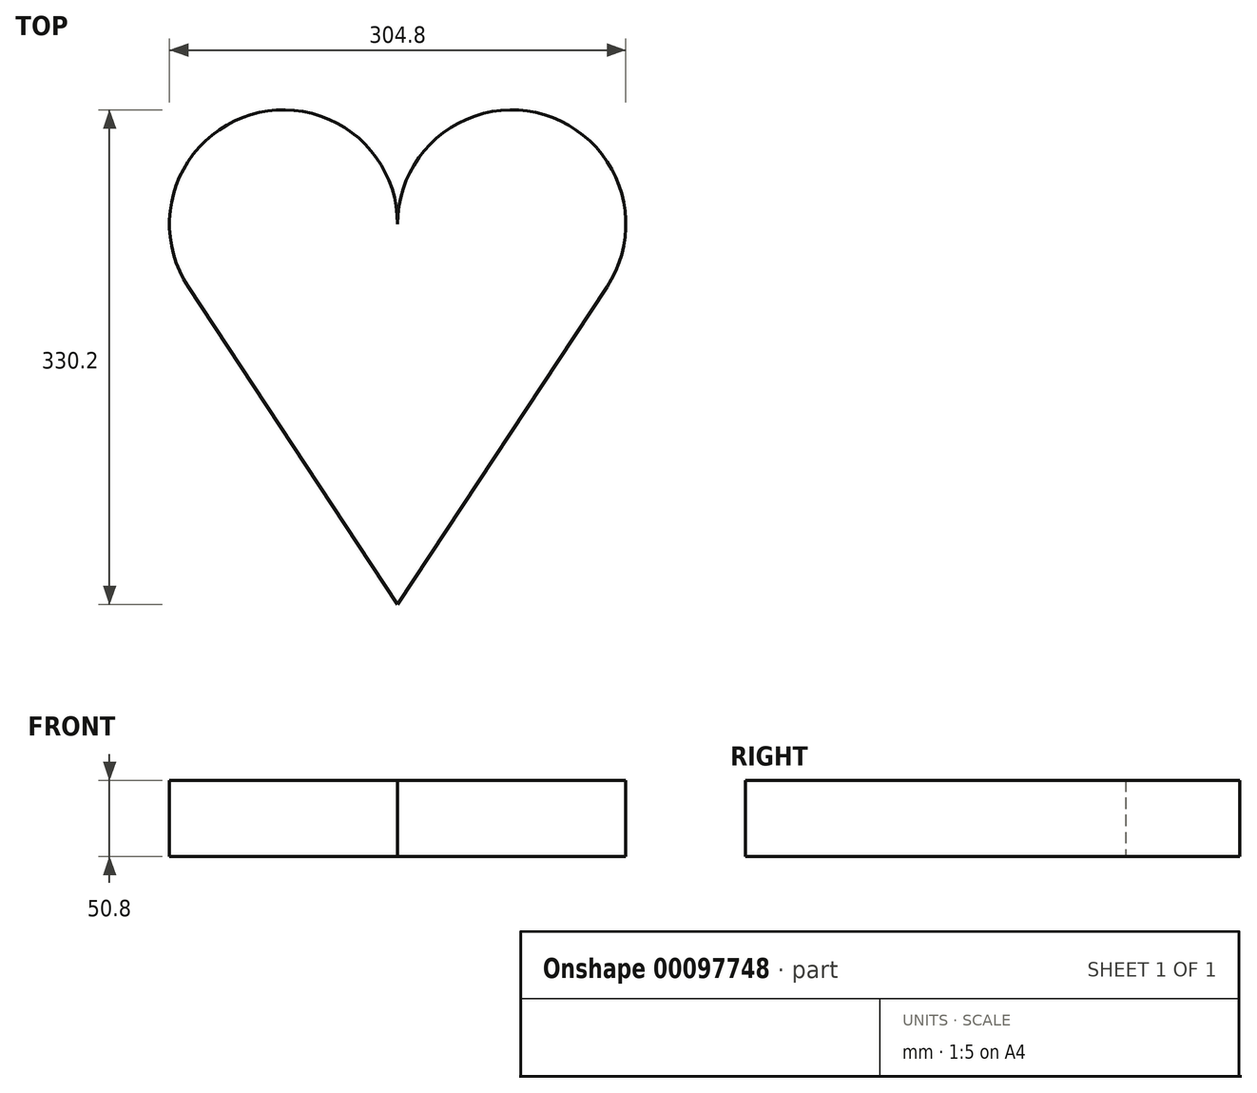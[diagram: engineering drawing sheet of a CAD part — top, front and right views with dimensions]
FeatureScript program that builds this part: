
annotation { "Feature Type Name" : "Feature", "Feature Type Description" : "" }
export const myFeature = defineFeature(function(context is Context, id is Id, definition is map)
    precondition{}
    {
        {
            var Q0;
            Q0=qCreatedBy(makeId("Top.planeOp"),FACE);
            var sketch = newSketch(context, id + "F0", { "sketchPlane" : qUnion([Q0])});
            skArc(sketch, "E0", {"start": v(0, 20.97) * mm, "mid": v(-49.05, 57.47) * mm, "end": v(-69.9, 0) * mm});
            skArc(sketch, "E1", {"start": v(69.9, 0) * mm, "mid": v(49.05, 57.47) * mm, "end": v(0, 20.97) * mm});
            skLineSegment(sketch, "E2", {"start": v(-69.9, 0) * mm, "end": v(0, -106.03) * mm});
            skLineSegment(sketch, "E3", {"start": v(0, -106.03) * mm, "end": v(69.9, 0) * mm});
            skLineSegment(sketch, "E4", {"start": v(-69.9, 0) * mm, "end": v(69.9, 0) * mm, "construction": true});
            skSolve(sketch);
        }
        {
            var Q0;
            Q0 = qSketchRegion(id + "F0", true);
            extrude(context, id + "F1", {"entities" : qUnion([Q0]), "depth" : 25.4 * mm});
        }
        {
            var Q0;
            Q0=makeQuery(id+"F1.opExtrude","SWEPT_BODY",BODY,{"disambiguationData":[OSD([sQuery(id+"F0.wireOp",EDGE,"E0"),sQuery(id+"F0.wireOp",EDGE,"E1"),sQuery(id+"F0.wireOp",EDGE,"E2"),sQuery(id+"F0.wireOp",EDGE,"E3")])]});
            var Q1;
            Q1=qCreatedBy(makeId("Origin.pointOp"),VERTEX);
            transform(context, id + "F2", {"entities" : qUnion([Q0]), "transformType" : TransformType.SCALE_UNIFORMLY, "scale" : 2, "scalePoint" : qUnion([Q1]), "makeCopy" : false});
        }
    });
